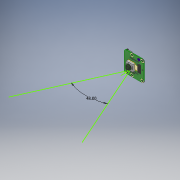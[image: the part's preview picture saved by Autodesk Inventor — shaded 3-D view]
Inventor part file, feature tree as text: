
AUTODESK INVENTOR PART (.ipt)
format: ipt  version: 2017 (Build 210142000, 142)  size: 4,356,608 bytes
history: native  units: in
note: dims shown in document units (in); Inventor stores cm internally (conversion verified against a paired STEP export)
features: other x129, sketch x2
ambient origin geometry x8: Origin, YZ Plane, XZ Plane, XY Plane, X Axis, Y Axis, Z Axis, Center Point
bodies: Solid1 (feature_tree), Solid2 (feature_tree), Solid3 (feature_tree), Solid4 (feature_tree), Solid5 (feature_tree), Solid6 (feature_tree), Solid7 (feature_tree), Solid8 (feature_tree), Solid9 (feature_tree), Solid10 (feature_tree), Solid11 (feature_tree), Solid12 (feature_tree), Solid13 (feature_tree), Solid14 (feature_tree), Solid15 (feature_tree), Solid16 (feature_tree), Solid17 (feature_tree), Solid18 (feature_tree), Solid19 (feature_tree), Solid20 (feature_tree), Solid21 (feature_tree), Solid22 (feature_tree), Solid23 (feature_tree), Solid24 (feature_tree), Solid25 (feature_tree), Solid26 (feature_tree), Solid27 (feature_tree), Solid28 (feature_tree), Solid29 (feature_tree), Solid30 (feature_tree), Solid31 (feature_tree), Solid32 (feature_tree), Solid33 (feature_tree), Solid34 (feature_tree), Solid35 (feature_tree), Solid36 (feature_tree), Solid37 (feature_tree), Solid38 (feature_tree), Solid39 (feature_tree), Solid40 (feature_tree), Solid41 (feature_tree), Solid42 (feature_tree), Solid43 (feature_tree), Solid44 (feature_tree), Solid45 (feature_tree), Solid46 (feature_tree), Solid47 (feature_tree), Solid48 (feature_tree), Solid49 (feature_tree), Solid50 (feature_tree), Solid51 (feature_tree), Solid52 (feature_tree), Solid53 (feature_tree), Solid54 (feature_tree), Solid55 (feature_tree), Solid56 (feature_tree), Solid57 (feature_tree), Solid58 (feature_tree), Solid59 (feature_tree), Solid60 (feature_tree), Solid61 (feature_tree), Solid62 (feature_tree), Solid63 (feature_tree), Solid64 (feature_tree), Solid65 (feature_tree), Solid66 (feature_tree), Solid67 (feature_tree), Solid68 (feature_tree), Solid69 (feature_tree), Solid70 (feature_tree), Solid71 (feature_tree), Solid72 (feature_tree), Solid73 (feature_tree), Solid74 (feature_tree), Solid75 (feature_tree), Solid76 (feature_tree), Solid77 (feature_tree), Solid78 (feature_tree), Solid79 (feature_tree), Solid80 (feature_tree), Solid81 (feature_tree), Solid82 (feature_tree), Solid83 (feature_tree), Solid84 (feature_tree), Solid85 (feature_tree), Solid86 (feature_tree), Solid87 (feature_tree), Solid88 (feature_tree), Solid89 (feature_tree), Solid90 (feature_tree), Solid91 (feature_tree), Solid92 (feature_tree), Solid93 (feature_tree), Solid94 (feature_tree), Solid95 (feature_tree), Solid96 (feature_tree), Solid97 (feature_tree), Solid98 (feature_tree), Solid99 (feature_tree), Solid100 (feature_tree), Solid101 (feature_tree), Solid102 (feature_tree), Solid103 (feature_tree), Solid104 (feature_tree), Solid105 (feature_tree), Solid106 (feature_tree), Solid107 (feature_tree), Solid108 (feature_tree), Solid109 (feature_tree), Solid110 (feature_tree), Solid111 (feature_tree), Solid112 (feature_tree), Solid113 (feature_tree), Solid114 (feature_tree), Solid115 (feature_tree), Solid116 (feature_tree), Solid117 (feature_tree), Solid118 (feature_tree), Solid119 (feature_tree), Solid120 (feature_tree), Solid121 (feature_tree), Solid122 (feature_tree), Solid123 (feature_tree), Solid124 (feature_tree), Solid125 (feature_tree), Solid126 (feature_tree), Solid127 (feature_tree), Solid128 (feature_tree), Solid129 (feature_tree), Solid130 (feature_tree), Solid131 (feature_tree), Solid132 (feature_tree), Solid133 (feature_tree)
feature tree (131):
  other  "Repaired Geometry1"
  sketch  "Sketch1"  dims[d0=0.3298in]
  sketch  "3D Sketch1"
  other  "PicameraPCB_1:1"
  other  "PicameraPCB_1:2"
  other  "PicameraPCB_1:3"
  other  "PicameraPCB_1:4"
  other  "PicameraPCB_1:5"
  other  "PicameraPCB_1:6"
  other  "PicameraPCB_1:7"
  other  "PicameraPCB_1:8"
  other  "PicameraPCB_1:9"
  other  "PicameraPCB_1:10"
  other  "PicameraPCB_1:11"
  other  "PicameraPCB_1:12"
  other  "PicameraPCB_1:13"
  other  "PicameraPCB_1:14"
  other  "PicameraPCB_1:15"
  other  "PicameraPCB_1:16"
  other  "PicameraPCB_1:17"
  other  "PicameraPCB_1:18"
  other  "PicameraPCB_1:19"
  other  "PicameraPCB_1:20"
  other  "PicameraPCB_1:21"
  other  "PicameraPCB_1:22"
  other  "PicameraPCB_1:23"
  other  "PicameraPCB_1:24"
  other  "PicameraPCB_1:25"
  other  "PicameraPCB_1:26"
  other  "PicameraPCB_1:27"
  other  "PicameraPCB_1:28"
  other  "PicameraPCB_1:29"
  other  "PicameraPCB_1:30"
  other  "PicameraPCB_1:31"
  other  "PicameraPCB_1:32"
  other  "PicameraPCB_1:33"
  other  "PicameraPCB_1:34"
  other  "PicameraPCB_1:35"
  other  "PicameraPCB_1:36"
  other  "PicameraPCB_1:37"
  other  "PicameraPCB_1:38"
  other  "PicameraPCB_1:39"
  other  "PicameraPCB_1:40"
  other  "PicameraPCB_1:41"
  other  "PicameraPCB_1:42"
  other  "PicameraPCB_1:43"
  other  "PicameraPCB_1:44"
  other  "PicameraPCB_1:45"
  other  "PicameraPCB_1:46"
  other  "PicameraPCB_1:47"
  other  "PicameraPCB_1:48"
  other  "PicameraPCB_1:49"
  other  "OVA5647_Housing_1:1"
  other  "OVA5647_Lens_FOV_1:1"
  other  "ribbon_cam_1:1"
  other  "CAPC-0805-T0.75-BN_1:1"
  other  "CAPC-0805-T0.75-BN_2:1"
  other  "CAPC-0402-T0.55-BN_1:1"
  other  "CAPC-0402-T0.55-BN_2:1"
  other  "CAPC-0402-T0.55-BN_3:1"
  other  "CAPC-0402-T0.55-BN_4:1"
  other  "CAPC-0402-T0.55-BN_5:1"
  other  "CAPC-0402-T0.55-BN_6:1"
  other  "CAPC-0402-T0.55-BN_7:1"
  other  "CAPC-0402-T0.55-BN_8:1"
  other  "CAPC-0402-T0.55-BN_9:1"
  other  "CAPC-0402-T0.55-BN_10:1"
  other  "RESC-0402_1:1"
  other  "RESC-0402_1:2"
  other  "RESC-0402_1:3"
  other  "RESC-0402_2:1"
  other  "RESC-0402_2:2"
  other  "RESC-0402_2:3"
  other  "RESC-0402_5:1"
  other  "RESC-0402_5:2"
  other  "RESC-0402_5:3"
  other  "RESC-0603_1:1"
  other  "RESC-0603_1:2"
  other  "RESC-0603_1:3"
  other  "RESC-0603_2:1"
  other  "RESC-0603_2:2"
  other  "RESC-0603_2:3"
  other  "RESC-1210_1:1"
  other  "RESC-1210_1:2"
  other  "RESC-1210_1:3"
  other  "c-1-1734248-5-e-raspberry_display_1:1"
  other  "SOT23-5_1:1"
  other  "SOT23-5_1:2"
  other  "SOT23-5_1:3"
  other  "SOT23-5_1:4"
  other  "SOT23-5_1:5"
  other  "SOT23-5_1:6"
  other  "SOT23-5_2:1"
  other  "SOT23-5_2:2"
  other  "SOT23-5_2:3"
  other  "SOT23-5_2:4"
  other  "SOT23-5_2:5"
  other  "SOT23-5_2:6"
  other  "SOT23-5_3:1"
  other  "SOT23-5_3:2"
  other  "SOT23-5_3:3"
  other  "SOT23-5_3:4"
  other  "SOT23-5_3:5"
  other  "SOT23-5_3:6"
  other  "KX7 SMD Quartz Crystal Resonator 3.2x2.5mm_4:1"
  other  "c6aaa_1:1"
  other  "c6aaa_1:2"
  other  "c6aaa_1:3"
  other  "c6aaa_1:4"
  other  "c6aaa_1:5"
  other  "c6aaa_1:6"
  other  "c6aaa_1:7"
  other  "c6aaa_1:8"
  other  "c6aaa_1:9"
  other  "4pin_smd_1:1"
  other  "4pin_smd_1:2"
  other  "4pin_smd_1:3"
  other  "4pin_smd_1:4"
  other  "4pin_smd_1:5"
  other  "4pin_smd_2:1"
  other  "4pin_smd_2:2"
  other  "4pin_smd_2:3"
  other  "4pin_smd_2:4"
  other  "4pin_smd_2:5"
  other  "4pin_smd_3:1"
  other  "4pin_smd_3:2"
  other  "4pin_smd_3:3"
  other  "4pin_smd_3:4"
  other  "4pin_smd_3:5"
  other  "Composite1"
  other  "Srf1"
